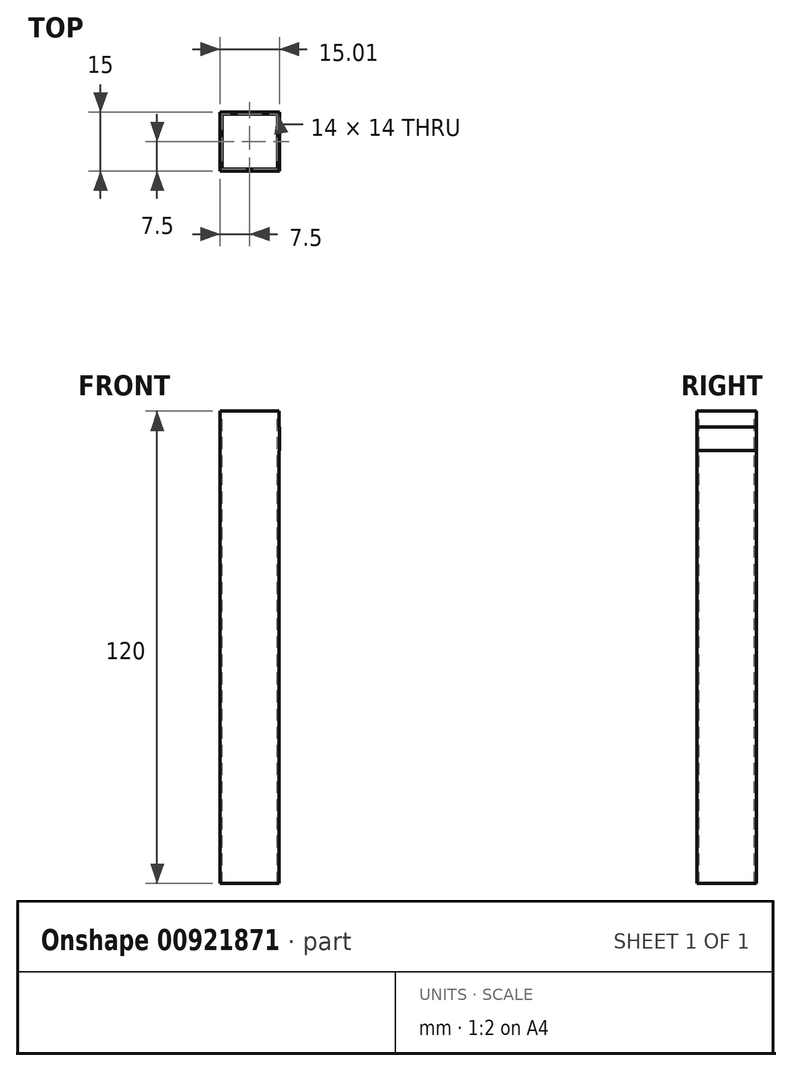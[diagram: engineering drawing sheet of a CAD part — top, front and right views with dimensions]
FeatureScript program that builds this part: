
annotation { "Feature Type Name" : "Feature", "Feature Type Description" : "" }
export const myFeature = defineFeature(function(context is Context, id is Id, definition is map)
    precondition{}
    {
        {
            var Q0;
            Q0=qCreatedBy(makeId("Top.planeOp"),FACE);
            var sketch = newSketch(context, id + "F0", { "sketchPlane" : qUnion([Q0])});
            skLineSegment(sketch, "E0.bottom", {"start": v(7.5, -7.5) * mm, "end": v(-7.5, -7.5) * mm});
            skLineSegment(sketch, "E0.top", {"start": v(7.5, 7.5) * mm, "end": v(-7.5, 7.5) * mm});
            skLineSegment(sketch, "E0.left", {"start": v(7.5, -7.5) * mm, "end": v(7.5, 7.5) * mm});
            skLineSegment(sketch, "E0.right", {"start": v(-7.5, -7.5) * mm, "end": v(-7.5, 7.5) * mm});
            skPoint(sketch, "E0.middle", {"position": v(0, 0) * mm});
            skLineSegment(sketch, "E1.bottom", {"start": v(7, -7) * mm, "end": v(-7, -7) * mm});
            skLineSegment(sketch, "E1.top", {"start": v(7, 7) * mm, "end": v(-7, 7) * mm});
            skLineSegment(sketch, "E1.left", {"start": v(7, -7) * mm, "end": v(7, 7) * mm});
            skLineSegment(sketch, "E1.right", {"start": v(-7, -7) * mm, "end": v(-7, 7) * mm});
            skSolve(sketch);
        }
        {
            var Q0;
            Q0=makeQuery(id+"F0.imprint","IMPRINT",FACE,{"disambiguationData":[TD([[makeQuery(id+"F0.imprint","IMPRINT",EDGE,{"derivedFrom":sQuery(id+"F0.wireOp",EDGE,"E0.bottom")}),-1.0]])]});
            extrude(context, id + "F1", {"entities" : qUnion([Q0]), "oppositeDirection" : true, "depth" : 60 * mm, "offsetDistance" : 25 * mm});
        }
        {
            var Q0;
            Q0=makeQuery(id+"F1.opExtrude","SWEPT_FACE",FACE,{"disambiguationData":[OSD([sQuery(id+"F0.wireOp",EDGE,"E0.left")])]});
            var sketch = newSketch(context, id + "F2", { "sketchPlane" : qUnion([Q0])});
            skLineSegment(sketch, "E2.bottom", {"start": v(-7.5, 0) * mm, "end": v(7.5, 0) * mm});
            skLineSegment(sketch, "E2.top", {"start": v(-7.5, -4) * mm, "end": v(7.5, -4) * mm});
            skLineSegment(sketch, "E2.left", {"start": v(-7.5, 0) * mm, "end": v(-7.5, -4) * mm});
            skLineSegment(sketch, "E2.right", {"start": v(7.5, 0) * mm, "end": v(7.5, -4) * mm});
            skLineSegment(sketch, "E3.top", {"start": v(-7.5, -10) * mm, "end": v(7.5, -10) * mm});
            skLineSegment(sketch, "E3.left", {"start": v(-7.5, -4) * mm, "end": v(-7.5, -10) * mm});
            skLineSegment(sketch, "E3.right", {"start": v(7.5, -4) * mm, "end": v(7.5, -10) * mm});
            skSolve(sketch);
        }
        {
            var Q0;
            Q0=makeQuery(id+"F2.imprint","IMPRINT",FACE,{"disambiguationData":[TD([[makeQuery(id+"F2.imprint","IMPRINT",EDGE,{"derivedFrom":sQuery(id+"F2.wireOp",EDGE,"E2.top")}),-1.0]])]});
            extrude(context, id + "F3", {"entities" : qUnion([Q0]), "operationType" : NewBodyOperationType.ADD, "depth" : 0.01 * mm, "offsetDistance" : 25 * mm});
        }
        {
            var Q0;
            Q0=makeQuery(id+"F1.opExtrude","CAP_FACE",FACE,{"disambiguationData":[OSD([sQuery(id+"F0.wireOp",EDGE,"E0.bottom"),sQuery(id+"F0.wireOp",EDGE,"E0.top"),sQuery(id+"F0.wireOp",EDGE,"E0.left"),sQuery(id+"F0.wireOp",EDGE,"E0.right"),sQuery(id+"F0.wireOp",EDGE,"E1.bottom"),sQuery(id+"F0.wireOp",EDGE,"E1.top"),sQuery(id+"F0.wireOp",EDGE,"E1.left"),sQuery(id+"F0.wireOp",EDGE,"E1.right")])],"isStart":false});
            extrude(context, id + "F4", {"entities" : qUnion([Q0]), "operationType" : NewBodyOperationType.ADD, "depth" : 60 * mm, "offsetDistance" : 25 * mm});
        }
    });
